# Revit family: Practibox_S_flush_mounting_cabinet_18_modules_réf_137006_to_137179
name_source: partatom
category: Equipement électrique
revit_build: Autodesk Revit 2018 (Build: 20170223_1515(x64)
units: mm (PartAtom-declared; Revit-internal decimal feet)

## family parameters
Basée sur le plan de construction = Non
Configuration du panneau = Deux colonnes, circuits au sein
Cote de connecteur circulaire = Utiliser le diamètre
Couper avec des vides une fois chargée = Non
Numéro OmniClass = 23.80.30.11.17
Partagée = Non
Point de calcul de pièce = Non
Titre OmniClass = Distribution Boards and Control Panels
Toujours verticalement = Oui
Type d'élément = Tableau de raccordement

## types (32) — shared parameters
Fabricant = "Legrand"
General Conditions of Use = https://export.legrand.com
URL = www.legrand.com
width = 436 mm  [stored 1.43045 ft]

## per-type parameters (varying)
| type | 1R | 2R | 3R | 4R | Ina | Terminal block E | Terminal block N | depth | door B 1 r | door B 2 r | door B 3 r | door B 4 r | door T 1 r | door T 2 r | door T 3 r | door T 4 r | door transparent | door white | height | size |
| Practibox_S_flush_mounting_cabinet_36_modules_137027 | Non | Oui | Non | Non | 90 A |  |  | 103 mm  [stored 0.337927 ft] | Non | Oui | Non | Non | Non | Non | Non | Non | Non | Oui | 385 mm  [stored 1.26312 ft] | 2 row |
| Practibox_S_flush_mounting_cabinet_54_modules_137028 | Non | Non | Oui | Non | 90 A |  |  | 103 mm  [stored 0.337927 ft] | Non | Non | Oui | Non | Non | Non | Non | Non | Non | Oui | 615 mm  [stored 2.01772 ft] | 3 row |
| Practibox_S_flush_mounting_cabinet_72_modules_137029 | Non | Non | Non | Oui | 90 A |  |  | 103 mm  [stored 0.337927 ft] | Non | Non | Non | Oui | Non | Non | Non | Non | Non | Oui | 765 mm  [stored 2.50984 ft] | 4 row |
| Practibox_S_flush_mounting_cabinet_18_modules_137026 | Oui | Non | Non | Non | 63 A |  |  | 102 mm | Oui | Non | Non | Non | Non | Non | Non | Non | Non | Oui | 235 mm  [stored 0.770997 ft] | 1 row |
| Practibox_S_flush_mounting_cabinet_18_modules_137036 | Oui | Non | Non | Non | 63 A |  |  | 102 mm | Non | Non | Non | Non | Oui | Non | Non | Non | Oui | Non | 235 mm  [stored 0.770997 ft] | 1 row |
| Practibox_S_flush_mounting_cabinet_18_modules_137176 | Oui | Non | Non | Non | 63 A | 17 connections Icc 10kA | 17 connections Icc 10kA | 102 mm | Non | Non | Non | Non | Oui | Non | Non | Non | Oui | Non | 235 mm  [stored 0.770997 ft] | 1 row |
| Practibox_S_flush_mounting_cabinet_18_modules_137166 | Oui | Non | Non | Non | 63 A | 17 connections Icc 10kA | 17 connections Icc 10kA | 102 mm | Oui | Non | Non | Non | Non | Non | Non | Non | Non | Oui | 235 mm  [stored 0.770997 ft] | 1 row |
| Practibox_S_flush_mounting_cabinet_36_modules_137037 | Non | Oui | Non | Non | 90 A |  |  | 103 mm  [stored 0.337927 ft] | Non | Non | Non | Non | Non | Oui | Non | Non | Oui | Non | 385 mm  [stored 1.26312 ft] | 2 row |
| Practibox_S_flush_mounting_cabinet_36_modules_137177 | Non | Oui | Non | Non | 90 A | 27 connections Icc 10kA | 27 connections Icc 10kA | 103 mm  [stored 0.337927 ft] | Non | Non | Non | Non | Non | Oui | Non | Non | Oui | Non | 385 mm  [stored 1.26312 ft] | 2 row |
| Practibox_S_flush_mounting_cabinet_36_modules_137167 | Non | Oui | Non | Non | 90 A | 27 connections Icc 10kA | 27 connections Icc 10kA | 103 mm  [stored 0.337927 ft] | Non | Oui | Non | Non | Non | Non | Non | Non | Non | Oui | 385 mm  [stored 1.26312 ft] | 2 row |
| Practibox_S_flush_mounting_cabinet_54_modules_137038 | Non | Non | Oui | Non | 90 A |  |  | 103 mm  [stored 0.337927 ft] | Non | Non | Non | Non | Non | Non | Oui | Non | Oui | Non | 615 mm  [stored 2.01772 ft] | 3 row |
| Practibox_S_flush_mounting_cabinet_54_modules_137168 | Non | Non | Oui | Non | 90 A | 27 connections Icc 10kA | 27 connections Icc 10kA | 103 mm  [stored 0.337927 ft] | Non | Non | Oui | Non | Non | Non | Non | Non | Non | Oui | 615 mm  [stored 2.01772 ft] | 3 row |
| Practibox_S_flush_mounting_cabinet_72_modules_137039 | Non | Non | Non | Oui | 90 A |  |  | 103 mm  [stored 0.337927 ft] | Non | Non | Non | Non | Non | Non | Non | Oui | Oui | Non | 765 mm  [stored 2.50984 ft] | 4 row |
| Practibox_S_flush_mounting_cabinet_72_modules_137169 | Non | Non | Non | Oui | 90 A | 27 connections Icc 10kA | 27 connections Icc 10kA | 103 mm  [stored 0.337927 ft] | Non | Non | Non | Oui | Non | Non | Non | Non | Non | Oui | 765 mm  [stored 2.50984 ft] | 4 row |
| Practibox_S_flush_mounting_cabinet_72_modules_137179 | Non | Non | Non | Oui | 90 A | 27 connections Icc 10kA | 27 connections Icc 10kA | 103 mm  [stored 0.337927 ft] | Non | Non | Non | Non | Non | Non | Non | Oui | Oui | Non | 765 mm  [stored 2.50984 ft] | 4 row |
| Practibox_S_flush_mounting_cabinet_18_modules_137006 | Oui | Non | Non | Non | 63 A |  |  | 102 mm | Oui | Non | Non | Non | Non | Non | Non | Non | Non | Oui | 235 mm  [stored 0.770997 ft] | 1 row |
| Practibox_S_flush_mounting_cabinet_18_modules_137016 | Oui | Non | Non | Non | 63 A |  |  | 102 mm | Non | Non | Non | Non | Oui | Non | Non | Non | Oui | Non | 235 mm  [stored 0.770997 ft] | 1 row |
| Practibox_S_flush_mounting_cabinet_18_modules_137156 | Oui | Non | Non | Non | 63 A | 17 connections Icc 10kA | 17 connections Icc 10kA | 102 mm | Non | Non | Non | Non | Oui | Non | Non | Non | Oui | Non | 235 mm  [stored 0.770997 ft] | 1 row |
| Practibox_S_flush_mounting_cabinet_18_modules_137146 | Oui | Non | Non | Non | 63 A | 17 connections Icc 10kA | 17 connections Icc 10kA | 102 mm | Oui | Non | Non | Non | Non | Non | Non | Non | Non | Oui | 235 mm  [stored 0.770997 ft] | 1 row |
| Practibox_S_flush_mounting_cabinet_36_modules_137007 | Non | Oui | Non | Non | 90 A |  |  | 103 mm  [stored 0.337927 ft] | Non | Oui | Non | Non | Non | Non | Non | Non | Non | Oui | 385 mm  [stored 1.26312 ft] | 2 row |
| Practibox_S_flush_mounting_cabinet_36_modules_137017 | Non | Oui | Non | Non | 90 A |  |  | 103 mm  [stored 0.337927 ft] | Non | Non | Non | Non | Non | Oui | Non | Non | Oui | Non | 385 mm  [stored 1.26312 ft] | 2 row |
| Practibox_S_flush_mounting_cabinet_36_modules_137157 | Non | Oui | Non | Non | 90 A | 27 connections Icc 10kA | 27 connections Icc 10kA | 103 mm  [stored 0.337927 ft] | Non | Non | Non | Non | Non | Oui | Non | Non | Oui | Non | 385 mm  [stored 1.26312 ft] | 2 row |
| Practibox_S_flush_mounting_cabinet_36_modules_137147 | Non | Oui | Non | Non | 90 A | 27 connections Icc 10kA | 27 connections Icc 10kA | 103 mm  [stored 0.337927 ft] | Non | Oui | Non | Non | Non | Non | Non | Non | Non | Oui | 385 mm  [stored 1.26312 ft] | 2 row |
| Practibox_S_flush_mounting_cabinet_54_modules_137008 | Non | Non | Oui | Non | 90 A |  |  | 103 mm  [stored 0.337927 ft] | Non | Non | Oui | Non | Non | Non | Non | Non | Non | Oui | 615 mm  [stored 2.01772 ft] | 3 row |
| Practibox_S_flush_mounting_cabinet_54_modules_137018 | Non | Non | Oui | Non | 90 A |  |  | 103 mm  [stored 0.337927 ft] | Non | Non | Non | Non | Non | Non | Oui | Non | Oui | Non | 615 mm  [stored 2.01772 ft] | 3 row |
| Practibox_S_flush_mounting_cabinet_54_modules_137158 | Non | Non | Oui | Non | 90 A | 27 connections Icc 10kA | 27 connections Icc 10kA | 103 mm  [stored 0.337927 ft] | Non | Non | Non | Non | Non | Non | Oui | Non | Oui | Non | 615 mm  [stored 2.01772 ft] | 3 row |
| Practibox_S_flush_mounting_cabinet_54_modules_137148 | Non | Non | Oui | Non | 90 A | 27 connections Icc 10kA | 27 connections Icc 10kA | 103 mm  [stored 0.337927 ft] | Non | Non | Oui | Non | Non | Non | Non | Non | Non | Oui | 615 mm  [stored 2.01772 ft] | 3 row |
| Practibox_S_flush_mounting_cabinet_72_modules_137009 | Non | Non | Non | Oui | 90 A |  |  | 103 mm  [stored 0.337927 ft] | Non | Non | Non | Oui | Non | Non | Non | Non | Non | Oui | 765 mm  [stored 2.50984 ft] | 4 row |
| Practibox_S_flush_mounting_cabinet_72_modules_137019 | Non | Non | Non | Oui | 90 A |  |  | 103 mm  [stored 0.337927 ft] | Non | Non | Non | Non | Non | Non | Non | Oui | Oui | Non | 765 mm  [stored 2.50984 ft] | 4 row |
| Practibox_S_flush_mounting_cabinet_72_modules_137159 | Non | Non | Non | Oui | 90 A | 27 connections Icc 10kA | 27 connections Icc 10kA | 103 mm  [stored 0.337927 ft] | Non | Non | Non | Non | Non | Non | Non | Oui | Oui | Non | 765 mm  [stored 2.50984 ft] | 4 row |
| Practibox_S_flush_mounting_cabinet_72_modules_137149 | Non | Non | Non | Oui | 90 A | 27 connections Icc 10kA | 27 connections Icc 10kA | 103 mm  [stored 0.337927 ft] | Non | Non | Non | Oui | Non | Non | Non | Non | Non | Oui | 765 mm  [stored 2.50984 ft] | 4 row |
| Practibox_S_flush_mounting_cabinet_54_modules_137178 | Non | Non | Oui | Non | 90 A | 27 connections Icc 10kA | 27 connections Icc 10kA | 103 mm  [stored 0.337927 ft] | Non | Non | Non | Non | Non | Non | Oui | Non | Oui | Non | 615 mm  [stored 2.01772 ft] | 3 row |

note: column(s) folded — value = type name in every type: Description

note: [stored X ft] marks values corroborated as IEEE doubles in the binary element streams (Revit-internal decimal feet)
